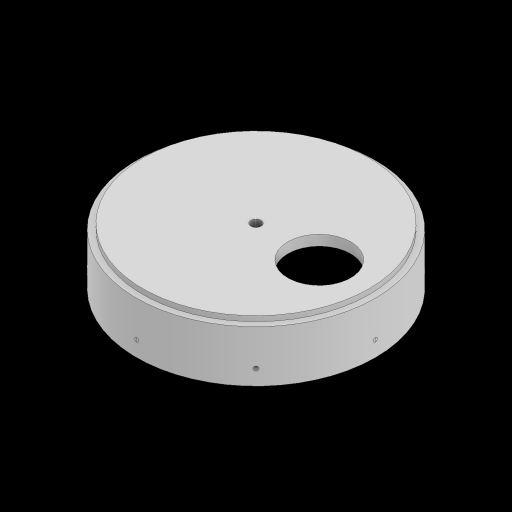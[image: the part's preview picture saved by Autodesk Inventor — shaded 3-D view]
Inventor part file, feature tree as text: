
AUTODESK INVENTOR PART (.ipt)
format: ipt  version: 2023 (Build 270158000, 158)  size: 185,344 bytes
history: native  units: in
note: dims shown in document units (in); Inventor stores cm internally (conversion verified against a paired STEP export)
features: extrude x5, sketch x4, pattern_circular x2, plane x1
ambient origin geometry x8: Origin, YZ Plane, XZ Plane, XY Plane, X Axis, Y Axis, Z Axis, Center Point
bodies: Solid1 (feature_tree)
feature tree (12):
  extrude  "Extrusion1"  Depth=5.5in
  extrude  "Extrusion2"  Depth=5.3125in
  extrude  "Extrusion3"  Depth=5.8in
  plane  "Work Plane1"
  sketch  "Sketch4"  dims[d14=1.25in d15=0.0in d16=2.9in d17=0.1in d19=0.75in d20=0.0in d21=3.1496in d22=360.0deg d24=1.0in d25=0.0in d26=1.5748in d27=360.0deg d30=0.375in d31=0.0344in d32=0.5in d33=0.0344in]
  extrude  "Extrusion4"  Depth=2.9in
  pattern_circular  "Circular Pattern1"  [2 undecoded]
  extrude  "Extrusion5"  Depth=2.9in TaperAngle=0.0deg
  pattern_circular  "Circular Pattern2"  Count=8 Angle=360.0deg
  sketch  "Sketch1"  dims[d1=1.5748in d2=5.125in d3=1.525in d4=1.5375in d5=360.0deg d6=0.25in d7=5.5in]
  sketch  "Sketch2"  dims[d8=0.75in d9=0.0in d10=5.3125in]
  sketch  "Sketch3"  dims[d11=0.5in d12=0.0in d13=5.8in]
note: 2 required parameter values undecoded (feature->parameter linkage not recoverable at this tier; creation-order binding heuristic only, values carry confidence <= 0.55)
